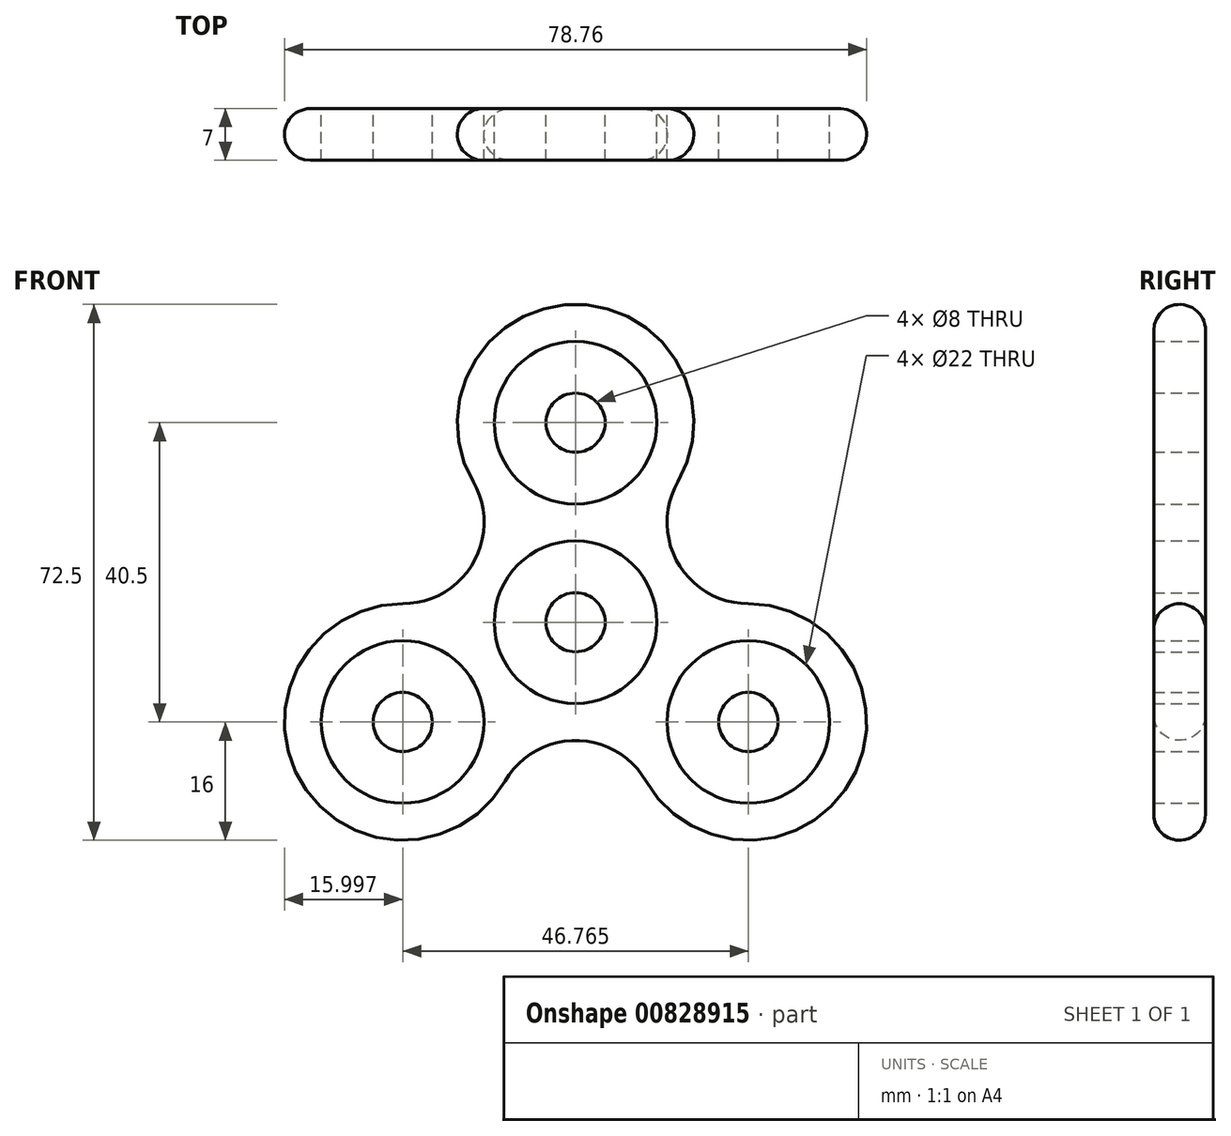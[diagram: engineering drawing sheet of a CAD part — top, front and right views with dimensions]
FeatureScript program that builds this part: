
annotation { "Feature Type Name" : "Feature", "Feature Type Description" : "" }
export const myFeature = defineFeature(function(context is Context, id is Id, definition is map)
    precondition{}
    {
        {
            assignVariable(context, id + "F0", {"name" : "Fillet", "anyValue" : 3.5});
        }
        {
            var Q0;
            Q0=qCreatedBy(makeId("Front.planeOp"),FACE);
            var sketch = newSketch(context, id + "F1", { "sketchPlane" : qUnion([Q0])});
            skCircle(sketch, "E0", {"center": v(0, 0) * mm, "radius": 11 * mm});
            skCircle(sketch, "E1", {"center": v(0, 0) * mm, "radius": 4 * mm});
            skSolve(sketch);
        }
        {
            var Q0;
            Q0=makeQuery(id+"F1.imprint","IMPRINT",FACE,{"disambiguationData":[TD([[makeQuery(id+"F1.imprint","IMPRINT",EDGE,{"derivedFrom":sQuery(id+"F1.wireOp",EDGE,"E0")}),1.0]])]});
            extrude(context, id + "F2", {"entities" : qUnion([Q0]), "endBound" : BoundingType.SYMMETRIC, "depth" : 7 * mm, "offsetDistance" : 25 * mm});
        }
        {
            var Q0;
            Q0=qCreatedBy(makeId("Front.planeOp"),FACE);
            var sketch = newSketch(context, id + "F3", { "sketchPlane" : qUnion([Q0])});
            skLineSegment(sketch, "E2", {"start": v(0, 0) * mm, "end": v(0, 40) * mm});
            skLineSegment(sketch, "E3", {"start": v(0, 16) * mm, "end": v(0, 27) * mm});
            skCircle(sketch, "E4", {"center": v(0, 27) * mm, "radius": 11 * mm});
            skCircle(sketch, "E5", {"center": v(0, 27) * mm, "radius": 4 * mm, "construction": true});
            skPoint(sketch, "E6.center", {"position": v(0, 0) * mm});
            skArc(sketch, "E7", {"start": v(13.86, 19) * mm, "mid": v(0, 43) * mm, "end": v(-13.86, 19) * mm});
            skLineSegment(sketch, "E8", {"start": v(0, 0) * mm, "end": v(0, 69.14) * mm});
            skLineSegment(sketch, "E9", {"start": v(0, 0) * mm, "end": v(-13.86, 8) * mm, "construction": true});
            skArc(sketch, "E10.filletArc", {"start": v(-13.86, 8) * mm, "mid": v(-12.38, 13.5) * mm, "end": v(-13.86, 19) * mm});
            skLineSegment(sketch, "E11", {"start": v(0, 0) * mm, "end": v(13.86, 8) * mm, "construction": true});
            skArc(sketch, "E12.filletArc", {"start": v(13.86, 19) * mm, "mid": v(12.38, 13.5) * mm, "end": v(13.86, 8) * mm});
            skCircle(sketch, "E13.1.0", {"center": v(-23.38, -13.5) * mm, "radius": 11 * mm});
            skCircle(sketch, "E13.1.1", {"center": v(-23.38, -13.5) * mm, "radius": 4 * mm, "construction": true});
            skArc(sketch, "E13.1.2", {"start": v(-23.38, 2.5) * mm, "mid": v(-37.24, -21.5) * mm, "end": v(-9.53, -21.5) * mm});
            skArc(sketch, "E13.1.3", {"start": v(0, -16) * mm, "mid": v(-5.5, -17.47) * mm, "end": v(-9.53, -21.5) * mm});
            skArc(sketch, "E13.1.4", {"start": v(-23.38, 2.5) * mm, "mid": v(-17.88, 3.97) * mm, "end": v(-13.86, 8) * mm});
            skCircle(sketch, "E13.2.0", {"center": v(23.38, -13.5) * mm, "radius": 11 * mm});
            skCircle(sketch, "E13.2.1", {"center": v(23.38, -13.5) * mm, "radius": 4 * mm, "construction": true});
            skArc(sketch, "E13.2.2", {"start": v(9.53, -21.5) * mm, "mid": v(37.24, -21.5) * mm, "end": v(23.38, 2.5) * mm});
            skArc(sketch, "E13.2.3", {"start": v(13.86, 8) * mm, "mid": v(17.88, 3.97) * mm, "end": v(23.38, 2.5) * mm});
            skArc(sketch, "E13.2.4", {"start": v(9.53, -21.5) * mm, "mid": v(5.5, -17.47) * mm, "end": v(0, -16) * mm});
            skCircle(sketch, "E14.0.0", {"center": v(0, 0) * mm, "radius": 11 * mm});
            skCircle(sketch, "E15.0", {"center": v(0, 0) * mm, "radius": 4 * mm});
            skSolve(sketch);
        }
        {
            var Q0;
            {var subQ5=sQuery(id+"F3.wireOp",EDGE,"E10.filletArc");Q0=makeQuery(id+"F3.imprint","IMPRINT",FACE,{"disambiguationData":[TD([[makeQuery(id+"F3.imprint","IMPRINT",EDGE,{"derivedFrom":subQ5}),-1.0]])]});}
            extrude(context, id + "F4", {"entities" : qUnion([Q0]), "endBound" : BoundingType.SYMMETRIC, "depth" : 7 * mm, "offsetDistance" : 25 * mm});
        }
        {
            var Q0;
            Q0=makeQuery(id+"F4.opExtrude","CAP_EDGE",EDGE,{"disambiguationData":[OSD([sQuery(id+"F3.wireOp",EDGE,"E13.1.2")])],"isStart":false});
            var Q1;
            Q1=makeQuery(id+"F4.opExtrude","CAP_EDGE",EDGE,{"disambiguationData":[OSD([sQuery(id+"F3.wireOp",EDGE,"E13.1.3"),sQuery(id+"F3.wireOp",EDGE,"E13.2.4")])],"isStart":false});
            var Q2;
            Q2=makeQuery(id+"F4.opExtrude","CAP_EDGE",EDGE,{"disambiguationData":[OSD([sQuery(id+"F3.wireOp",EDGE,"E13.2.2")])],"isStart":false});
            var Q3;
            Q3=makeQuery(id+"F4.opExtrude","CAP_EDGE",EDGE,{"disambiguationData":[OSD([sQuery(id+"F3.wireOp",EDGE,"E12.filletArc"),sQuery(id+"F3.wireOp",EDGE,"E13.2.3")])],"isStart":false});
            var Q4;
            Q4=makeQuery(id+"F4.opExtrude","CAP_EDGE",EDGE,{"disambiguationData":[OSD([sQuery(id+"F3.wireOp",EDGE,"E7")])],"isStart":false});
            var Q5;
            Q5=makeQuery(id+"F4.opExtrude","CAP_EDGE",EDGE,{"disambiguationData":[OSD([sQuery(id+"F3.wireOp",EDGE,"E10.filletArc"),sQuery(id+"F3.wireOp",EDGE,"E13.1.4")])],"isStart":false});
            var Q6;
            Q6=makeQuery(id+"F4.opExtrude","CAP_EDGE",EDGE,{"disambiguationData":[OSD([sQuery(id+"F3.wireOp",EDGE,"E13.1.3"),sQuery(id+"F3.wireOp",EDGE,"E13.2.4")])],"isStart":true});
            var Q7;
            Q7=makeQuery(id+"F4.opExtrude","CAP_EDGE",EDGE,{"disambiguationData":[OSD([sQuery(id+"F3.wireOp",EDGE,"E13.2.2")])],"isStart":true});
            var Q8;
            Q8=makeQuery(id+"F4.opExtrude","CAP_EDGE",EDGE,{"disambiguationData":[OSD([sQuery(id+"F3.wireOp",EDGE,"E13.1.2")])],"isStart":true});
            var Q9;
            Q9=makeQuery(id+"F4.opExtrude","CAP_EDGE",EDGE,{"disambiguationData":[OSD([sQuery(id+"F3.wireOp",EDGE,"E7")])],"isStart":true});
            var Q10;
            Q10=makeQuery(id+"F4.opExtrude","CAP_EDGE",EDGE,{"disambiguationData":[OSD([sQuery(id+"F3.wireOp",EDGE,"E12.filletArc"),sQuery(id+"F3.wireOp",EDGE,"E13.2.3")])],"isStart":true});
            var Q11;
            Q11=makeQuery(id+"F4.opExtrude","CAP_EDGE",EDGE,{"disambiguationData":[OSD([sQuery(id+"F3.wireOp",EDGE,"E10.filletArc"),sQuery(id+"F3.wireOp",EDGE,"E13.1.4")])],"isStart":true});
            fillet(context, id + "F5", {"entities" : qUnion([Q0, Q1, Q2, Q3, Q4, Q5, Q6, Q7, Q8, Q9, Q10, Q11]), "radius" : (getVariable(context, 'Fillet')) * mm, "tangentPropagation" : true, "allowEdgeOverflow" : false});
        }
        {
            var Q0;
            Q0=makeQuery(id+"F2.opExtrude","SWEPT_BODY",BODY,{"disambiguationData":[OSD([sQuery(id+"F1.wireOp",EDGE,"E0"),sQuery(id+"F1.wireOp",EDGE,"E1")])]});
            transform(context, id + "F6", {"entities" : qUnion([Q0]), "transformType" : TransformType.TRANSLATION_3D, "dx" : 0 * mm, "dy" : 0 * mm, "dz" : 27 * mm, "makeCopy" : true});
        }
        {
            var Q0;
            Q0=makeQuery(id+"F6.opPattern","COPY",BODY,{"derivedFrom":makeQuery(id+"F2.opExtrude","SWEPT_BODY",BODY,{"disambiguationData":[OSD([sQuery(id+"F1.wireOp",EDGE,"E0"),sQuery(id+"F1.wireOp",EDGE,"E1")])]}),"instanceName":"1"});
            var Q1;
            Q1=makeQuery(id+"F2.opExtrude","CAP_EDGE",EDGE,{"disambiguationData":[OSD([sQuery(id+"F1.wireOp",EDGE,"E0")])],"isStart":false});
            circularPattern(context, id + "F7", {"entities" : qUnion([Q0]), "axis" : qUnion([Q1]), "angle" : 360 * degree, "instanceCount" : 3, "equalSpace" : true});
        }
    });
